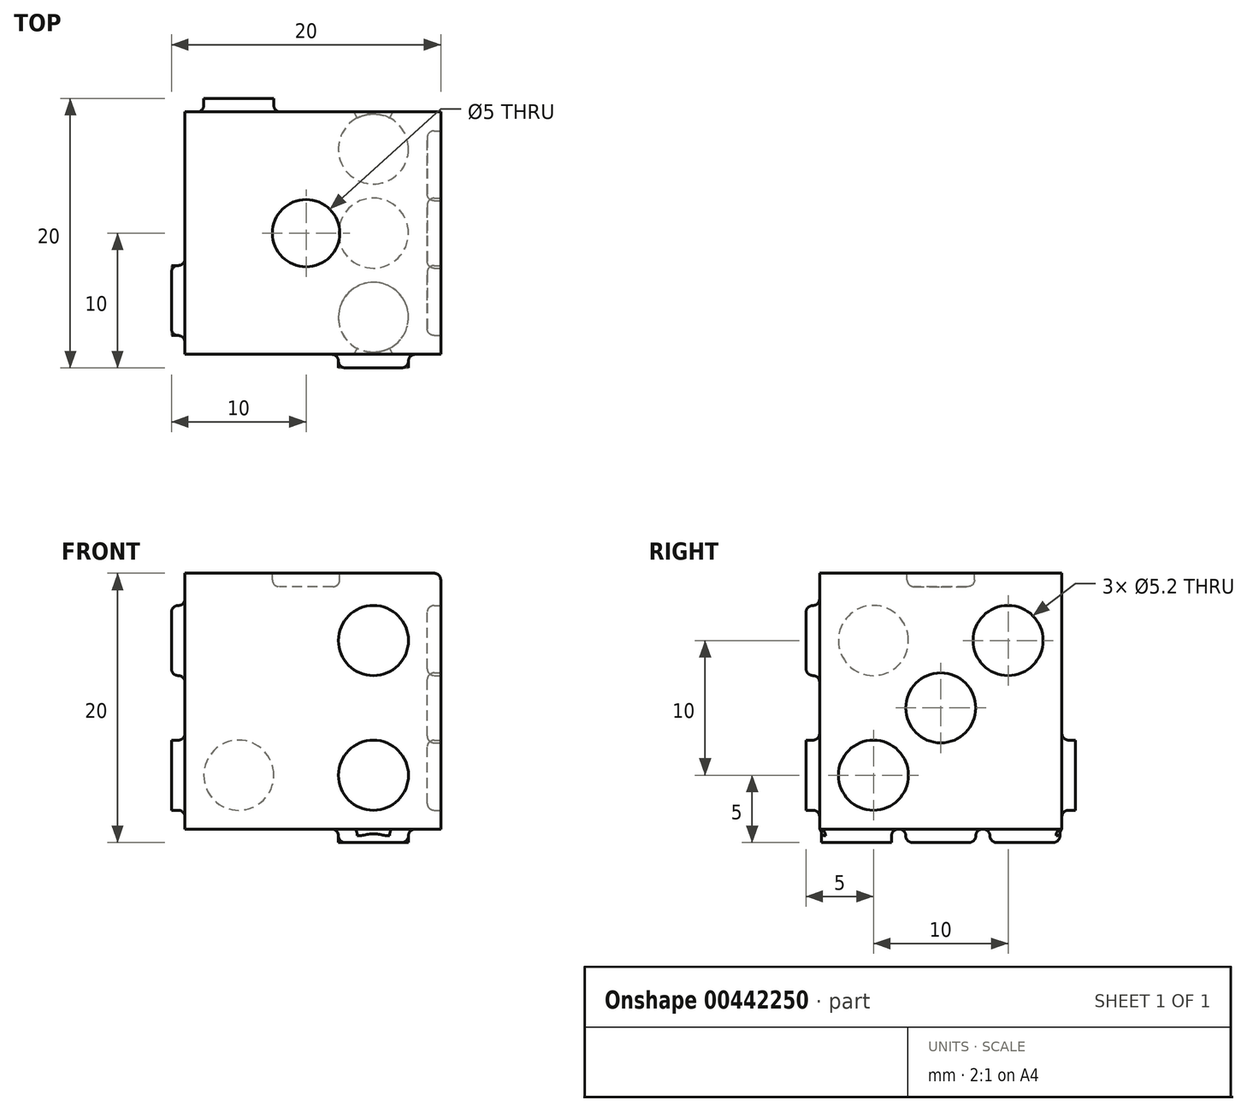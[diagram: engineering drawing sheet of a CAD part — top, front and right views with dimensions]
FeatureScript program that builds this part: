
annotation { "Feature Type Name" : "Feature", "Feature Type Description" : "" }
export const myFeature = defineFeature(function(context is Context, id is Id, definition is map)
    precondition{}
    {
        {
            var Q0;
            Q0=qCreatedBy(makeId("Front.planeOp"),FACE);
            var sketch = newSketch(context, id + "F0", { "sketchPlane" : qUnion([Q0])});
            skLineSegment(sketch, "E0.bottom", {"start": v(0, 0) * mm, "end": v(20, 0) * mm});
            skLineSegment(sketch, "E0.top", {"start": v(0, 20) * mm, "end": v(20, 20) * mm});
            skLineSegment(sketch, "E0.left", {"start": v(0, 0) * mm, "end": v(0, 20) * mm});
            skLineSegment(sketch, "E0.right", {"start": v(20, 0) * mm, "end": v(20, 20) * mm});
            skSolve(sketch);
        }
        {
            var Q0;
            Q0=makeQuery(id+"F0.imprint","IMPRINT",FACE,{"disambiguationData":[TD([[makeQuery(id+"F0.imprint","IMPRINT",EDGE,{"derivedFrom":sQuery(id+"F0.wireOp",EDGE,"E0.bottom")}),1.0]])]});
            extrude(context, id + "F1", {"entities" : qUnion([Q0]), "depth" : 20 * mm});
        }
        {
            var Q0;
            Q0=makeQuery(id+"F1.opExtrude","CAP_FACE",FACE,{"disambiguationData":[OSD([sQuery(id+"F0.wireOp",EDGE,"E0.bottom"),sQuery(id+"F0.wireOp",EDGE,"E0.top"),sQuery(id+"F0.wireOp",EDGE,"E0.left"),sQuery(id+"F0.wireOp",EDGE,"E0.right")])],"isStart":false});
            var sketch = newSketch(context, id + "F2", { "sketchPlane" : qUnion([Q0])});
            skLineSegment(sketch, "E1", {"start": v(0, 20) * mm, "end": v(20, 0) * mm, "construction": true});
            skLineSegment(sketch, "E2", {"start": v(0, 0) * mm, "end": v(20, 20) * mm, "construction": true});
            skCircle(sketch, "E3", {"center": v(10, 10) * mm, "radius": 2.6 * mm});
            skCircle(sketch, "E4", {"center": v(5, 15) * mm, "radius": 2.6 * mm});
            skCircle(sketch, "E5.MirrorC", {"center": v(15, 5) * mm, "radius": 2.6 * mm});
            skLineSegment(sketch, "E6", {"start": v(10, 10) * mm, "end": v(10, 0) * mm, "construction": true});
            skCircle(sketch, "E7.MirrorC", {"center": v(5, 5) * mm, "radius": 2.6 * mm});
            skCircle(sketch, "E8.MirrorC", {"center": v(15, 15) * mm, "radius": 2.6 * mm});
            skSolve(sketch);
        }
        {
            var Q0;
            Q0=makeQuery(id+"F2.imprint","IMPRINT",FACE,{"disambiguationData":[TD([[makeQuery(id+"F2.imprint","IMPRINT",EDGE,{"derivedFrom":sQuery(id+"F2.wireOp",EDGE,"E4")}),1.0]])]});
            var Q1;
            Q1=makeQuery(id+"F2.imprint","IMPRINT",FACE,{"disambiguationData":[TD([[makeQuery(id+"F2.imprint","IMPRINT",EDGE,{"derivedFrom":sQuery(id+"F2.wireOp",EDGE,"E7.MirrorC")}),1.0]])]});
            var Q2;
            Q2=makeQuery(id+"F2.imprint","IMPRINT",FACE,{"disambiguationData":[TD([[makeQuery(id+"F2.imprint","IMPRINT",EDGE,{"derivedFrom":sQuery(id+"F2.wireOp",EDGE,"E3")}),1.0]])]});
            var Q3;
            Q3=makeQuery(id+"F2.imprint","IMPRINT",FACE,{"disambiguationData":[TD([[makeQuery(id+"F2.imprint","IMPRINT",EDGE,{"derivedFrom":sQuery(id+"F2.wireOp",EDGE,"E5.MirrorC")}),-1.0]])]});
            var Q4;
            Q4=makeQuery(id+"F2.imprint","IMPRINT",FACE,{"disambiguationData":[TD([[makeQuery(id+"F2.imprint","IMPRINT",EDGE,{"derivedFrom":sQuery(id+"F2.wireOp",EDGE,"E8.MirrorC")}),-1.0]])]});
            extrude(context, id + "F3", {"entities" : qUnion([Q0, Q1, Q2, Q3, Q4]), "operationType" : NewBodyOperationType.REMOVE, "oppositeDirection" : true, "depth" : 1 * mm});
        }
        {
            var Q0;
            Q0=makeQuery(id+"F3.boolean.opBoolean","COPY",EDGE,{"derivedFrom":makeQuery(id+"F3.opExtrude","CAP_EDGE",EDGE,{"disambiguationData":[OSD([sQuery(id+"F2.wireOp",EDGE,"E3")])],"isStart":true})});
            var Q1;
            Q1=makeQuery(id+"F3.boolean.opBoolean","COPY",EDGE,{"derivedFrom":makeQuery(id+"F3.opExtrude","CAP_EDGE",EDGE,{"disambiguationData":[OSD([sQuery(id+"F2.wireOp",EDGE,"E3")])],"isStart":false})});
            var Q2;
            Q2=makeQuery(id+"F3.boolean.opBoolean","COPY",EDGE,{"derivedFrom":makeQuery(id+"F3.opExtrude","CAP_EDGE",EDGE,{"disambiguationData":[OSD([sQuery(id+"F2.wireOp",EDGE,"E7.MirrorC")])],"isStart":true})});
            var Q3;
            Q3=makeQuery(id+"F3.boolean.opBoolean","COPY",EDGE,{"derivedFrom":makeQuery(id+"F3.opExtrude","CAP_EDGE",EDGE,{"disambiguationData":[OSD([sQuery(id+"F2.wireOp",EDGE,"E7.MirrorC")])],"isStart":false})});
            var Q4;
            Q4=makeQuery(id+"F3.boolean.opBoolean","COPY",EDGE,{"derivedFrom":makeQuery(id+"F3.opExtrude","CAP_EDGE",EDGE,{"disambiguationData":[OSD([sQuery(id+"F2.wireOp",EDGE,"E5.MirrorC")])],"isStart":true})});
            var Q5;
            Q5=makeQuery(id+"F3.boolean.opBoolean","COPY",EDGE,{"derivedFrom":makeQuery(id+"F3.opExtrude","CAP_EDGE",EDGE,{"disambiguationData":[OSD([sQuery(id+"F2.wireOp",EDGE,"E5.MirrorC")])],"isStart":false})});
            var Q6;
            Q6=makeQuery(id+"F3.boolean.opBoolean","COPY",EDGE,{"derivedFrom":makeQuery(id+"F3.opExtrude","CAP_EDGE",EDGE,{"disambiguationData":[OSD([sQuery(id+"F2.wireOp",EDGE,"E8.MirrorC")])],"isStart":false})});
            var Q7;
            Q7=makeQuery(id+"F3.boolean.opBoolean","COPY",EDGE,{"derivedFrom":makeQuery(id+"F3.opExtrude","CAP_EDGE",EDGE,{"disambiguationData":[OSD([sQuery(id+"F2.wireOp",EDGE,"E8.MirrorC")])],"isStart":true})});
            var Q8;
            Q8=makeQuery(id+"F3.boolean.opBoolean","COPY",EDGE,{"derivedFrom":makeQuery(id+"F3.opExtrude","CAP_EDGE",EDGE,{"disambiguationData":[OSD([sQuery(id+"F2.wireOp",EDGE,"E4")])],"isStart":true})});
            var Q9;
            Q9=makeQuery(id+"F3.boolean.opBoolean","COPY",EDGE,{"derivedFrom":makeQuery(id+"F3.opExtrude","CAP_EDGE",EDGE,{"disambiguationData":[OSD([sQuery(id+"F2.wireOp",EDGE,"E4")])],"isStart":false})});
            fillet(context, id + "F4", {"entities" : qUnion([Q0, Q1, Q2, Q3, Q4, Q5, Q6, Q7, Q8, Q9]), "radius" : 0.5 * mm, "tangentPropagation" : true, "allowEdgeOverflow" : false});
        }
        {
            var Q0;
            Q0=makeQuery(id+"F1.opExtrude","CAP_FACE",FACE,{"disambiguationData":[OSD([sQuery(id+"F0.wireOp",EDGE,"E0.bottom"),sQuery(id+"F0.wireOp",EDGE,"E0.top"),sQuery(id+"F0.wireOp",EDGE,"E0.left"),sQuery(id+"F0.wireOp",EDGE,"E0.right")])],"isStart":true});
            var sketch = newSketch(context, id + "F5", { "sketchPlane" : qUnion([Q0])});
            skLineSegment(sketch, "E9", {"start": v(-20, 20) * mm, "end": v(0, 0) * mm, "construction": true});
            skCircle(sketch, "E10", {"center": v(-15, 15) * mm, "radius": 2.6 * mm});
            skLineSegment(sketch, "E11", {"start": v(-20, 0) * mm, "end": v(0, 20) * mm, "construction": true});
            skCircle(sketch, "E12.MirrorC", {"center": v(-5, 5) * mm, "radius": 2.6 * mm});
            skSolve(sketch);
        }
        {
            var Q0;
            Q0=makeQuery(id+"F5.imprint","IMPRINT",FACE,{"disambiguationData":[TD([[makeQuery(id+"F5.imprint","IMPRINT",EDGE,{"derivedFrom":sQuery(id+"F5.wireOp",EDGE,"E10")}),1.0]])]});
            var Q1;
            Q1=makeQuery(id+"F5.imprint","IMPRINT",FACE,{"disambiguationData":[TD([[makeQuery(id+"F5.imprint","IMPRINT",EDGE,{"derivedFrom":sQuery(id+"F5.wireOp",EDGE,"E12.MirrorC")}),-1.0]])]});
            extrude(context, id + "F6", {"entities" : qUnion([Q0, Q1]), "operationType" : NewBodyOperationType.REMOVE, "oppositeDirection" : true, "depth" : 1 * mm});
        }
        {
            var Q0;
            Q0=makeQuery(id+"F6.boolean.opBoolean","COPY",EDGE,{"derivedFrom":makeQuery(id+"F6.opExtrude","CAP_EDGE",EDGE,{"disambiguationData":[OSD([sQuery(id+"F5.wireOp",EDGE,"E10")])],"isStart":true})});
            var Q1;
            Q1=makeQuery(id+"F6.boolean.opBoolean","COPY",EDGE,{"derivedFrom":makeQuery(id+"F6.opExtrude","CAP_EDGE",EDGE,{"disambiguationData":[OSD([sQuery(id+"F5.wireOp",EDGE,"E10")])],"isStart":false})});
            var Q2;
            Q2=makeQuery(id+"F6.boolean.opBoolean","COPY",EDGE,{"derivedFrom":makeQuery(id+"F6.opExtrude","CAP_EDGE",EDGE,{"disambiguationData":[OSD([sQuery(id+"F5.wireOp",EDGE,"E12.MirrorC")])],"isStart":true})});
            var Q3;
            Q3=makeQuery(id+"F6.boolean.opBoolean","COPY",EDGE,{"derivedFrom":makeQuery(id+"F6.opExtrude","CAP_EDGE",EDGE,{"disambiguationData":[OSD([sQuery(id+"F5.wireOp",EDGE,"E12.MirrorC")])],"isStart":false})});
            fillet(context, id + "F7", {"entities" : qUnion([Q0, Q1, Q2, Q3]), "radius" : 0.5 * mm, "tangentPropagation" : true, "allowEdgeOverflow" : false});
        }
        {
            var Q0;
            Q0=makeQuery(id+"F1.opExtrude","SWEPT_FACE",FACE,{"disambiguationData":[OSD([sQuery(id+"F0.wireOp",EDGE,"E0.top")])]});
            var sketch = newSketch(context, id + "F8", { "sketchPlane" : qUnion([Q0])});
            skLineSegment(sketch, "E13", {"start": v(0, 0) * mm, "end": v(20, -20) * mm, "construction": true});
            skLineSegment(sketch, "E14", {"start": v(0, -20) * mm, "end": v(20, 0) * mm, "construction": true});
            skCircle(sketch, "E15", {"center": v(10, -10) * mm, "radius": 2.5 * mm});
            skSolve(sketch);
        }
        {
            var Q0;
            Q0=makeQuery(id+"F8.imprint","IMPRINT",FACE,{"disambiguationData":[TD([[makeQuery(id+"F8.imprint","IMPRINT",EDGE,{"derivedFrom":sQuery(id+"F8.wireOp",EDGE,"E15")}),1.0]])]});
            extrude(context, id + "F9", {"entities" : qUnion([Q0]), "operationType" : NewBodyOperationType.REMOVE, "oppositeDirection" : true, "depth" : 1 * mm});
        }
        {
            var Q0;
            Q0=makeQuery(id+"F9.boolean.opBoolean","COPY",EDGE,{"derivedFrom":makeQuery(id+"F9.opExtrude","CAP_EDGE",EDGE,{"disambiguationData":[OSD([sQuery(id+"F8.wireOp",EDGE,"E15")])],"isStart":true})});
            var Q1;
            Q1=makeQuery(id+"F9.boolean.opBoolean","COPY",EDGE,{"derivedFrom":makeQuery(id+"F9.opExtrude","CAP_EDGE",EDGE,{"disambiguationData":[OSD([sQuery(id+"F8.wireOp",EDGE,"E15")])],"isStart":false})});
            fillet(context, id + "F10", {"entities" : qUnion([Q0, Q1]), "radius" : 0.5 * mm, "tangentPropagation" : true, "allowEdgeOverflow" : false});
        }
        {
            var Q0;
            Q0=makeQuery(id+"F1.opExtrude","SWEPT_FACE",FACE,{"disambiguationData":[OSD([sQuery(id+"F0.wireOp",EDGE,"E0.bottom")])]});
            var sketch = newSketch(context, id + "F11", { "sketchPlane" : qUnion([Q0])});
            skLineSegment(sketch, "E16", {"start": v(0, 20) * mm, "end": v(10, 20) * mm, "construction": true});
            skLineSegment(sketch, "E17", {"start": v(0, 0) * mm, "end": v(10, 0) * mm, "construction": true});
            skLineSegment(sketch, "E18", {"start": v(10, 20) * mm, "end": v(10, 0) * mm, "construction": true});
            skCircle(sketch, "E19", {"center": v(5, 16.25) * mm, "radius": 2.6 * mm});
            skCircle(sketch, "E20", {"center": v(5, 10) * mm, "radius": 2.6 * mm});
            skCircle(sketch, "E21", {"center": v(5, 3.75) * mm, "radius": 2.6 * mm});
            skCircle(sketch, "E22.MirrorC", {"center": v(15, 16.25) * mm, "radius": 2.6 * mm});
            skCircle(sketch, "E23.MirrorC", {"center": v(15, 10) * mm, "radius": 2.6 * mm});
            skCircle(sketch, "E24.MirrorC", {"center": v(15, 3.75) * mm, "radius": 2.6 * mm});
            skSolve(sketch);
        }
        {
            var Q0;
            Q0=makeQuery(id+"F11.imprint","IMPRINT",FACE,{"disambiguationData":[TD([[makeQuery(id+"F11.imprint","IMPRINT",EDGE,{"derivedFrom":sQuery(id+"F11.wireOp",EDGE,"E21")}),1.0]])]});
            var Q1;
            Q1=makeQuery(id+"F11.imprint","IMPRINT",FACE,{"disambiguationData":[TD([[makeQuery(id+"F11.imprint","IMPRINT",EDGE,{"derivedFrom":sQuery(id+"F11.wireOp",EDGE,"E20")}),1.0]])]});
            var Q2;
            Q2=makeQuery(id+"F11.imprint","IMPRINT",FACE,{"disambiguationData":[TD([[makeQuery(id+"F11.imprint","IMPRINT",EDGE,{"derivedFrom":sQuery(id+"F11.wireOp",EDGE,"E19")}),1.0]])]});
            var Q3;
            Q3=makeQuery(id+"F11.imprint","IMPRINT",FACE,{"disambiguationData":[TD([[makeQuery(id+"F11.imprint","IMPRINT",EDGE,{"derivedFrom":sQuery(id+"F11.wireOp",EDGE,"E22.MirrorC")}),-1.0]])]});
            var Q4;
            Q4=makeQuery(id+"F11.imprint","IMPRINT",FACE,{"disambiguationData":[TD([[makeQuery(id+"F11.imprint","IMPRINT",EDGE,{"derivedFrom":sQuery(id+"F11.wireOp",EDGE,"E23.MirrorC")}),-1.0]])]});
            var Q5;
            Q5=makeQuery(id+"F11.imprint","IMPRINT",FACE,{"disambiguationData":[TD([[makeQuery(id+"F11.imprint","IMPRINT",EDGE,{"derivedFrom":sQuery(id+"F11.wireOp",EDGE,"E24.MirrorC")}),-1.0]])]});
            extrude(context, id + "F12", {"entities" : qUnion([Q0, Q1, Q2, Q3, Q4, Q5]), "operationType" : NewBodyOperationType.REMOVE, "oppositeDirection" : true, "depth" : 1 * mm});
        }
        {
            var Q0;
            Q0=makeQuery(id+"F12.boolean.opBoolean","COPY",EDGE,{"derivedFrom":makeQuery(id+"F12.opExtrude","CAP_EDGE",EDGE,{"disambiguationData":[OSD([sQuery(id+"F11.wireOp",EDGE,"E19")])],"isStart":true})});
            var Q1;
            Q1=makeQuery(id+"F12.boolean.opBoolean","COPY",EDGE,{"derivedFrom":makeQuery(id+"F12.opExtrude","CAP_EDGE",EDGE,{"disambiguationData":[OSD([sQuery(id+"F11.wireOp",EDGE,"E19")])],"isStart":false})});
            var Q2;
            Q2=makeQuery(id+"F12.boolean.opBoolean","COPY",EDGE,{"derivedFrom":makeQuery(id+"F12.opExtrude","CAP_EDGE",EDGE,{"disambiguationData":[OSD([sQuery(id+"F11.wireOp",EDGE,"E20")])],"isStart":true})});
            var Q3;
            Q3=makeQuery(id+"F12.boolean.opBoolean","COPY",EDGE,{"derivedFrom":makeQuery(id+"F12.opExtrude","CAP_EDGE",EDGE,{"disambiguationData":[OSD([sQuery(id+"F11.wireOp",EDGE,"E20")])],"isStart":false})});
            var Q4;
            Q4=makeQuery(id+"F12.boolean.opBoolean","COPY",EDGE,{"derivedFrom":makeQuery(id+"F12.opExtrude","CAP_EDGE",EDGE,{"disambiguationData":[OSD([sQuery(id+"F11.wireOp",EDGE,"E21")])],"isStart":true})});
            var Q5;
            Q5=makeQuery(id+"F12.boolean.opBoolean","COPY",EDGE,{"derivedFrom":makeQuery(id+"F12.opExtrude","CAP_EDGE",EDGE,{"disambiguationData":[OSD([sQuery(id+"F11.wireOp",EDGE,"E21")])],"isStart":false})});
            var Q6;
            Q6=makeQuery(id+"F12.boolean.opBoolean","COPY",EDGE,{"derivedFrom":makeQuery(id+"F12.opExtrude","CAP_EDGE",EDGE,{"disambiguationData":[OSD([sQuery(id+"F11.wireOp",EDGE,"E22.MirrorC")])],"isStart":true})});
            var Q7;
            Q7=makeQuery(id+"F12.boolean.opBoolean","COPY",EDGE,{"derivedFrom":makeQuery(id+"F12.opExtrude","CAP_EDGE",EDGE,{"disambiguationData":[OSD([sQuery(id+"F11.wireOp",EDGE,"E22.MirrorC")])],"isStart":false})});
            var Q8;
            Q8=makeQuery(id+"F12.boolean.opBoolean","COPY",EDGE,{"derivedFrom":makeQuery(id+"F12.opExtrude","CAP_EDGE",EDGE,{"disambiguationData":[OSD([sQuery(id+"F11.wireOp",EDGE,"E23.MirrorC")])],"isStart":true})});
            var Q9;
            Q9=makeQuery(id+"F12.boolean.opBoolean","COPY",EDGE,{"derivedFrom":makeQuery(id+"F12.opExtrude","CAP_EDGE",EDGE,{"disambiguationData":[OSD([sQuery(id+"F11.wireOp",EDGE,"E23.MirrorC")])],"isStart":false})});
            var Q10;
            Q10=makeQuery(id+"F12.boolean.opBoolean","COPY",EDGE,{"derivedFrom":makeQuery(id+"F12.opExtrude","CAP_EDGE",EDGE,{"disambiguationData":[OSD([sQuery(id+"F11.wireOp",EDGE,"E24.MirrorC")])],"isStart":true})});
            var Q11;
            Q11=makeQuery(id+"F12.boolean.opBoolean","COPY",EDGE,{"derivedFrom":makeQuery(id+"F12.opExtrude","CAP_EDGE",EDGE,{"disambiguationData":[OSD([sQuery(id+"F11.wireOp",EDGE,"E24.MirrorC")])],"isStart":false})});
            fillet(context, id + "F13", {"entities" : qUnion([Q0, Q1, Q2, Q3, Q4, Q5, Q6, Q7, Q8, Q9, Q10, Q11]), "radius" : 0.5 * mm, "tangentPropagation" : true, "allowEdgeOverflow" : false});
        }
        {
            var Q0;
            Q0=makeQuery(id+"F1.opExtrude","SWEPT_FACE",FACE,{"disambiguationData":[OSD([sQuery(id+"F0.wireOp",EDGE,"E0.right")])]});
            var sketch = newSketch(context, id + "F14", { "sketchPlane" : qUnion([Q0])});
            skLineSegment(sketch, "E25", {"start": v(-20, 20) * mm, "end": v(0, 0) * mm, "construction": true});
            skLineSegment(sketch, "E26", {"start": v(0, 20) * mm, "end": v(-20, 0) * mm, "construction": true});
            skCircle(sketch, "E27", {"center": v(-10, 10) * mm, "radius": 2.6 * mm});
            skCircle(sketch, "E28", {"center": v(-5, 15) * mm, "radius": 2.6 * mm});
            skCircle(sketch, "E29", {"center": v(-15, 5) * mm, "radius": 2.6 * mm});
            skSolve(sketch);
        }
        {
            var Q0;
            Q0=makeQuery(id+"F14.imprint","IMPRINT",FACE,{"disambiguationData":[TD([[makeQuery(id+"F14.imprint","IMPRINT",EDGE,{"derivedFrom":sQuery(id+"F14.wireOp",EDGE,"E28")}),1.0]])]});
            var Q1;
            Q1=makeQuery(id+"F14.imprint","IMPRINT",FACE,{"disambiguationData":[TD([[makeQuery(id+"F14.imprint","IMPRINT",EDGE,{"derivedFrom":sQuery(id+"F14.wireOp",EDGE,"E27")}),1.0]])]});
            var Q2;
            Q2=makeQuery(id+"F14.imprint","IMPRINT",FACE,{"disambiguationData":[TD([[makeQuery(id+"F14.imprint","IMPRINT",EDGE,{"derivedFrom":sQuery(id+"F14.wireOp",EDGE,"E29")}),1.0]])]});
            extrude(context, id + "F15", {"entities" : qUnion([Q0, Q1, Q2]), "operationType" : NewBodyOperationType.REMOVE, "oppositeDirection" : true, "depth" : 1 * mm});
        }
        {
            var Q0;
            Q0=makeQuery(id+"F15.boolean.opBoolean","COPY",EDGE,{"derivedFrom":makeQuery(id+"F15.opExtrude","CAP_EDGE",EDGE,{"disambiguationData":[OSD([sQuery(id+"F14.wireOp",EDGE,"E28")])],"isStart":true})});
            var Q1;
            Q1=makeQuery(id+"F15.boolean.opBoolean","COPY",EDGE,{"derivedFrom":makeQuery(id+"F15.opExtrude","CAP_EDGE",EDGE,{"disambiguationData":[OSD([sQuery(id+"F14.wireOp",EDGE,"E28")])],"isStart":false})});
            var Q2;
            Q2=makeQuery(id+"F15.boolean.opBoolean","COPY",EDGE,{"derivedFrom":makeQuery(id+"F15.opExtrude","CAP_EDGE",EDGE,{"disambiguationData":[OSD([sQuery(id+"F14.wireOp",EDGE,"E27")])],"isStart":true})});
            var Q3;
            Q3=makeQuery(id+"F15.boolean.opBoolean","COPY",EDGE,{"derivedFrom":makeQuery(id+"F15.opExtrude","CAP_EDGE",EDGE,{"disambiguationData":[OSD([sQuery(id+"F14.wireOp",EDGE,"E27")])],"isStart":false})});
            var Q4;
            Q4=makeQuery(id+"F15.boolean.opBoolean","COPY",EDGE,{"derivedFrom":makeQuery(id+"F15.opExtrude","CAP_EDGE",EDGE,{"disambiguationData":[OSD([sQuery(id+"F14.wireOp",EDGE,"E29")])],"isStart":false})});
            var Q5;
            Q5=makeQuery(id+"F15.boolean.opBoolean","COPY",EDGE,{"derivedFrom":makeQuery(id+"F15.opExtrude","CAP_EDGE",EDGE,{"disambiguationData":[OSD([sQuery(id+"F14.wireOp",EDGE,"E29")])],"isStart":true})});
            fillet(context, id + "F16", {"entities" : qUnion([Q0, Q1, Q2, Q3, Q4, Q5]), "radius" : 0.5 * mm, "tangentPropagation" : true, "allowEdgeOverflow" : false});
        }
        {
            var Q0;
            Q0=makeQuery(id+"F1.opExtrude","SWEPT_FACE",FACE,{"disambiguationData":[OSD([sQuery(id+"F0.wireOp",EDGE,"E0.left")])]});
            var sketch = newSketch(context, id + "F17", { "sketchPlane" : qUnion([Q0])});
            skLineSegment(sketch, "E30", {"start": v(0, 20) * mm, "end": v(20, 0) * mm, "construction": true});
            skLineSegment(sketch, "E31", {"start": v(20, 20) * mm, "end": v(0, 0) * mm, "construction": true});
            skCircle(sketch, "E32", {"center": v(5, 15) * mm, "radius": 2.6 * mm});
            skCircle(sketch, "E33.MirrorC", {"center": v(15, 5) * mm, "radius": 2.6 * mm});
            skLineSegment(sketch, "E34", {"start": v(10, 10) * mm, "end": v(10, 0) * mm, "construction": true});
            skCircle(sketch, "E35.MirrorC", {"center": v(5, 5) * mm, "radius": 2.6 * mm});
            skCircle(sketch, "E36.MirrorC", {"center": v(15, 15) * mm, "radius": 2.6 * mm});
            skSolve(sketch);
        }
        {
            var Q0;
            Q0=makeQuery(id+"F17.imprint","IMPRINT",FACE,{"disambiguationData":[TD([[makeQuery(id+"F17.imprint","IMPRINT",EDGE,{"derivedFrom":sQuery(id+"F17.wireOp",EDGE,"E32")}),1.0]])]});
            var Q1;
            Q1=makeQuery(id+"F17.imprint","IMPRINT",FACE,{"disambiguationData":[TD([[makeQuery(id+"F17.imprint","IMPRINT",EDGE,{"derivedFrom":sQuery(id+"F17.wireOp",EDGE,"E35.MirrorC")}),1.0]])]});
            var Q2;
            Q2=makeQuery(id+"F17.imprint","IMPRINT",FACE,{"disambiguationData":[TD([[makeQuery(id+"F17.imprint","IMPRINT",EDGE,{"derivedFrom":sQuery(id+"F17.wireOp",EDGE,"E33.MirrorC")}),-1.0]])]});
            var Q3;
            Q3=makeQuery(id+"F17.imprint","IMPRINT",FACE,{"disambiguationData":[TD([[makeQuery(id+"F17.imprint","IMPRINT",EDGE,{"derivedFrom":sQuery(id+"F17.wireOp",EDGE,"E36.MirrorC")}),-1.0]])]});
            extrude(context, id + "F18", {"entities" : qUnion([Q0, Q1, Q2, Q3]), "operationType" : NewBodyOperationType.REMOVE, "oppositeDirection" : true, "depth" : 1 * mm});
        }
        {
            var Q0;
            Q0=makeQuery(id+"F18.boolean.opBoolean","COPY",EDGE,{"derivedFrom":makeQuery(id+"F18.opExtrude","CAP_EDGE",EDGE,{"disambiguationData":[OSD([sQuery(id+"F17.wireOp",EDGE,"E32")])],"isStart":true})});
            var Q1;
            Q1=makeQuery(id+"F18.boolean.opBoolean","COPY",EDGE,{"derivedFrom":makeQuery(id+"F18.opExtrude","CAP_EDGE",EDGE,{"disambiguationData":[OSD([sQuery(id+"F17.wireOp",EDGE,"E32")])],"isStart":false})});
            var Q2;
            Q2=makeQuery(id+"F18.boolean.opBoolean","COPY",EDGE,{"derivedFrom":makeQuery(id+"F18.opExtrude","CAP_EDGE",EDGE,{"disambiguationData":[OSD([sQuery(id+"F17.wireOp",EDGE,"E36.MirrorC")])],"isStart":true})});
            var Q3;
            Q3=makeQuery(id+"F18.boolean.opBoolean","COPY",EDGE,{"derivedFrom":makeQuery(id+"F18.opExtrude","CAP_EDGE",EDGE,{"disambiguationData":[OSD([sQuery(id+"F17.wireOp",EDGE,"E36.MirrorC")])],"isStart":false})});
            var Q4;
            Q4=makeQuery(id+"F18.boolean.opBoolean","COPY",EDGE,{"derivedFrom":makeQuery(id+"F18.opExtrude","CAP_EDGE",EDGE,{"disambiguationData":[OSD([sQuery(id+"F17.wireOp",EDGE,"E35.MirrorC")])],"isStart":true})});
            var Q5;
            Q5=makeQuery(id+"F18.boolean.opBoolean","COPY",EDGE,{"derivedFrom":makeQuery(id+"F18.opExtrude","CAP_EDGE",EDGE,{"disambiguationData":[OSD([sQuery(id+"F17.wireOp",EDGE,"E35.MirrorC")])],"isStart":false})});
            var Q6;
            Q6=makeQuery(id+"F18.boolean.opBoolean","COPY",EDGE,{"derivedFrom":makeQuery(id+"F18.opExtrude","CAP_EDGE",EDGE,{"disambiguationData":[OSD([sQuery(id+"F17.wireOp",EDGE,"E33.MirrorC")])],"isStart":true})});
            var Q7;
            Q7=makeQuery(id+"F18.boolean.opBoolean","COPY",EDGE,{"derivedFrom":makeQuery(id+"F18.opExtrude","CAP_EDGE",EDGE,{"disambiguationData":[OSD([sQuery(id+"F17.wireOp",EDGE,"E33.MirrorC")])],"isStart":false})});
            fillet(context, id + "F19", {"entities" : qUnion([Q0, Q1, Q2, Q3, Q4, Q5, Q6, Q7]), "radius" : 0.5 * mm, "tangentPropagation" : true, "allowEdgeOverflow" : false});
        }
        {
            var Q0;
            Q0=makeQuery(id+"F1.opExtrude","CAP_EDGE",EDGE,{"disambiguationData":[OSD([sQuery(id+"F0.wireOp",EDGE,"E0.left")])],"isStart":false});
            var Q1;
            Q1=makeQuery(id+"F1.opExtrude","SWEPT_EDGE",EDGE,{"disambiguationData":[OSD([sQuery(id+"F0.wireOp",EDGE,"E0.top"),sQuery(id+"F0.wireOp",EDGE,"E0.left")])]});
            var Q2;
            Q2=makeQuery(id+"F1.opExtrude","CAP_EDGE",EDGE,{"disambiguationData":[OSD([sQuery(id+"F0.wireOp",EDGE,"E0.top")])],"isStart":false});
            var Q3;
            Q3=makeQuery(id+"F1.opExtrude","SWEPT_EDGE",EDGE,{"disambiguationData":[OSD([sQuery(id+"F0.wireOp",EDGE,"E0.bottom"),sQuery(id+"F0.wireOp",EDGE,"E0.left")])]});
            var Q4;
            Q4=makeQuery(id+"F1.opExtrude","CAP_EDGE",EDGE,{"disambiguationData":[OSD([sQuery(id+"F0.wireOp",EDGE,"E0.bottom")])],"isStart":false});
            var Q5;
            Q5=makeQuery(id+"F1.opExtrude","CAP_EDGE",EDGE,{"disambiguationData":[OSD([sQuery(id+"F0.wireOp",EDGE,"E0.right")])],"isStart":false});
            var Q6;
            Q6=makeQuery(id+"F1.opExtrude","SWEPT_EDGE",EDGE,{"disambiguationData":[OSD([sQuery(id+"F0.wireOp",EDGE,"E0.bottom"),sQuery(id+"F0.wireOp",EDGE,"E0.right")])]});
            var Q7;
            Q7=makeQuery(id+"F1.opExtrude","CAP_EDGE",EDGE,{"disambiguationData":[OSD([sQuery(id+"F0.wireOp",EDGE,"E0.bottom")])],"isStart":true});
            var Q8;
            Q8=makeQuery(id+"F1.opExtrude","CAP_EDGE",EDGE,{"disambiguationData":[OSD([sQuery(id+"F0.wireOp",EDGE,"E0.right")])],"isStart":true});
            var Q9;
            Q9=makeQuery(id+"F1.opExtrude","CAP_EDGE",EDGE,{"disambiguationData":[OSD([sQuery(id+"F0.wireOp",EDGE,"E0.left")])],"isStart":true});
            var Q10;
            Q10=makeQuery(id+"F1.opExtrude","CAP_EDGE",EDGE,{"disambiguationData":[OSD([sQuery(id+"F0.wireOp",EDGE,"E0.top")])],"isStart":true});
            var Q11;
            Q11=makeQuery(id+"F1.opExtrude","SWEPT_EDGE",EDGE,{"disambiguationData":[OSD([sQuery(id+"F0.wireOp",EDGE,"E0.top"),sQuery(id+"F0.wireOp",EDGE,"E0.right")])]});
            fillet(context, id + "F20", {"entities" : qUnion([Q0, Q1, Q2, Q3, Q4, Q5, Q6, Q7, Q8, Q9, Q10, Q11]), "radius" : 0.5 * mm, "tangentPropagation" : true, "allowEdgeOverflow" : false});
        }
    });
